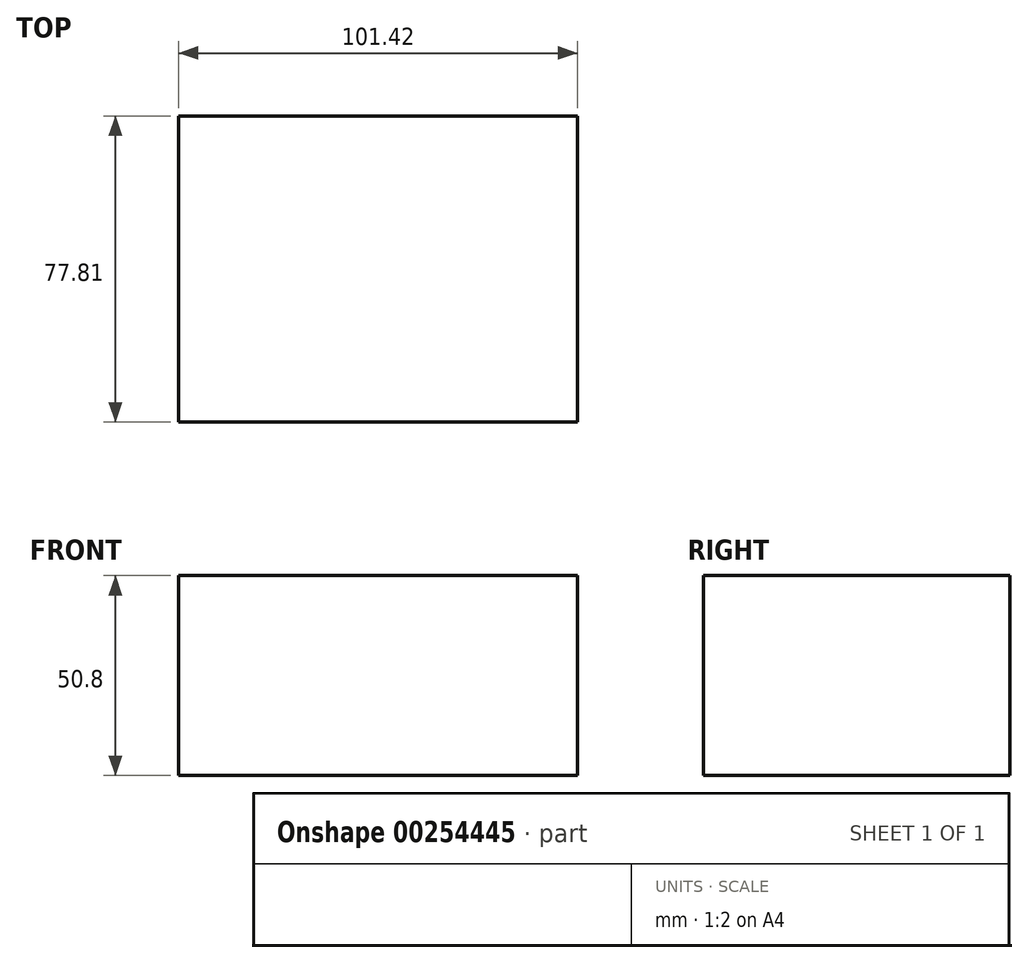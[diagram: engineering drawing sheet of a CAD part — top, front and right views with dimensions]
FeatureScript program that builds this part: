
annotation { "Feature Type Name" : "Feature", "Feature Type Description" : "" }
export const myFeature = defineFeature(function(context is Context, id is Id, definition is map)
    precondition{}
    {
        {
            var Q0;
            Q0=qCreatedBy(makeId("Top.planeOp"),FACE);
            var sketch = newSketch(context, id + "F0", { "sketchPlane" : qUnion([Q0])});
            skLineSegment(sketch, "E0.bottom", {"start": v(-48.03, 42.63) * mm, "end": v(53.39, 42.63) * mm});
            skLineSegment(sketch, "E0.top", {"start": v(-48.03, -35.18) * mm, "end": v(53.39, -35.18) * mm});
            skLineSegment(sketch, "E0.left", {"start": v(-48.03, 42.63) * mm, "end": v(-48.03, -35.18) * mm});
            skLineSegment(sketch, "E0.right", {"start": v(53.39, 42.63) * mm, "end": v(53.39, -35.18) * mm});
            skSolve(sketch);
        }
        {
            var Q0;
            Q0=makeQuery(id+"F0.imprint","IMPRINT",FACE,{"disambiguationData":[TD([[makeQuery(id+"F0.imprint","IMPRINT",EDGE,{"derivedFrom":sQuery(id+"F0.wireOp",EDGE,"E0.bottom")}),-1.0]])]});
            extrude(context, id + "F1", {"entities" : qUnion([Q0]), "depth" : 50.8 * mm});
        }
    });
